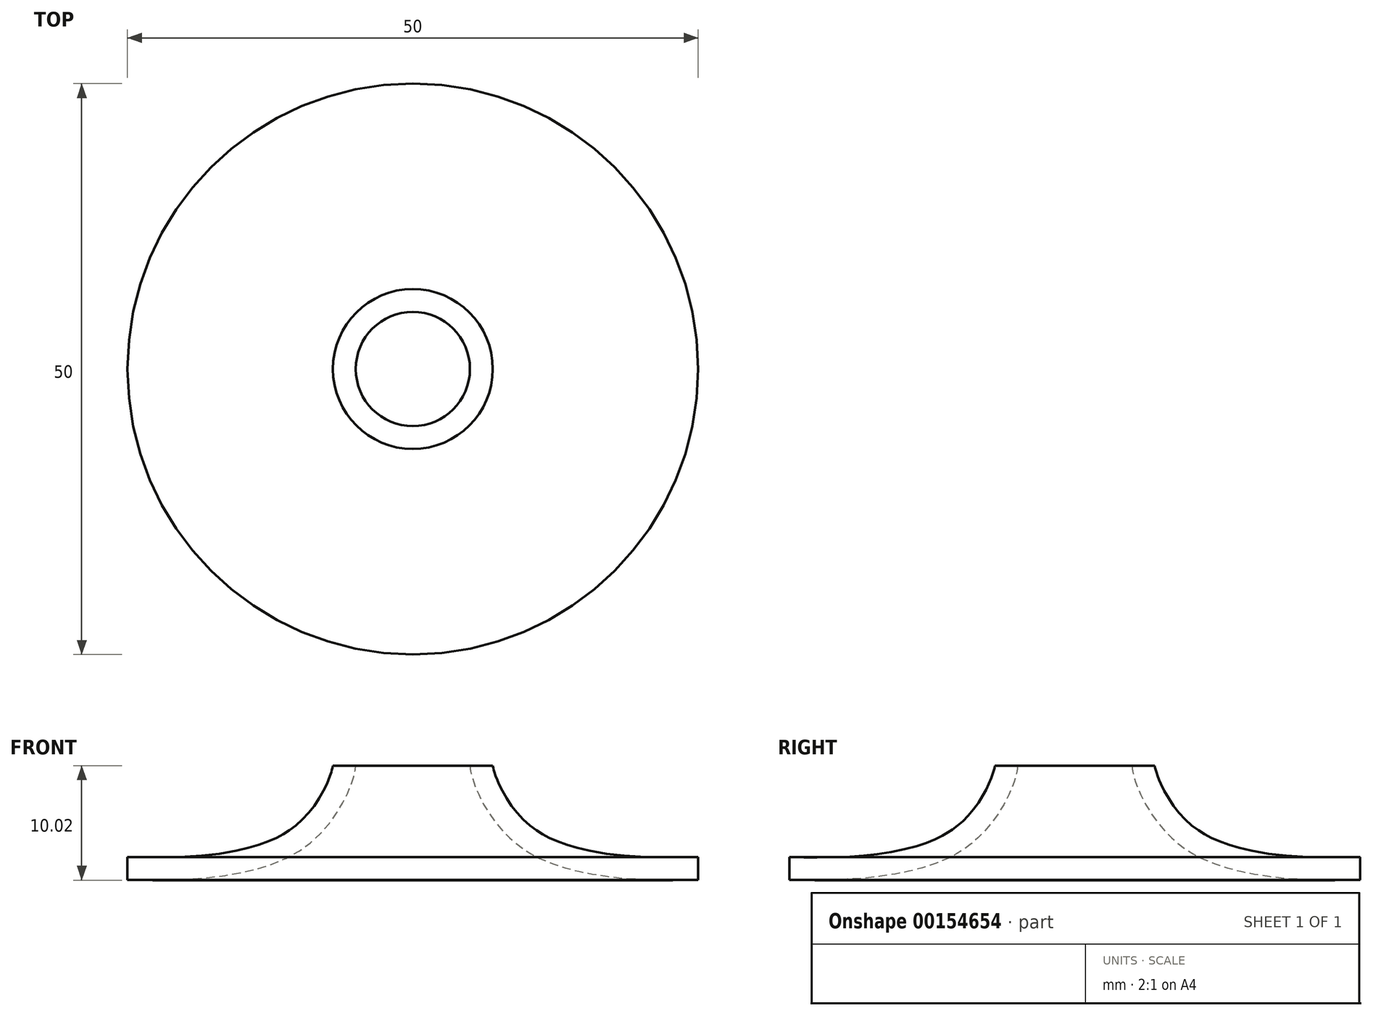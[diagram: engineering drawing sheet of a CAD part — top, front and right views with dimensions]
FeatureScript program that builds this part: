
annotation { "Feature Type Name" : "Feature", "Feature Type Description" : "" }
export const myFeature = defineFeature(function(context is Context, id is Id, definition is map)
    precondition{}
    {
        {
            var Q0;
            Q0=qCreatedBy(makeId("Right.planeOp"),FACE);
            var sketch = newSketch(context, id + "F0", { "sketchPlane" : qUnion([Q0])});
            skLineSegment(sketch, "E0", {"start": v(-25, 0) * mm, "end": v(0, 0) * mm, "construction": true});
            skLineSegment(sketch, "E1", {"start": v(0, 0) * mm, "end": v(0, 10) * mm, "construction": true});
            skLineSegment(sketch, "E2", {"start": v(-5, 0) * mm, "end": v(-5, 10) * mm, "construction": true});
            skFitSpline(sketch, "E3", {"points": [v(-25, 0) * mm, v(-10, 2.5) * mm, v(-5, 10) * mm], "startDerivative": vector(10.62, 0) * mm, "endDerivative": vector(0, 6.9) * mm});
            skFitSpline(sketch, "E4.0", {"points": [v(-25, 2) * mm, v(-24.87, 2) * mm, v(-24.6, 2) * mm, v(-23.94, 1.99) * mm, v(-22.91, 1.97) * mm, v(-21.4, 1.99) * mm, v(-19.12, 2.08) * mm, v(-16.6, 2.34) * mm, v(-14.2, 2.87) * mm, v(-12.82, 3.32) * mm, v(-11.84, 3.75) * mm, v(-11.29, 4.05) * mm, v(-10.89, 4.3) * mm, v(-10.5, 4.58) * mm, v(-10.04, 4.95) * mm, v(-9.54, 5.43) * mm, v(-8.92, 6.12) * mm, v(-8.4, 6.84) * mm, v(-7.97, 7.57) * mm, v(-7.69, 8.1) * mm, v(-7.46, 8.6) * mm, v(-7.27, 9.06) * mm, v(-7.14, 9.47) * mm, v(-7.06, 9.74) * mm, v(-7.03, 9.89) * mm, v(-7.01, 9.95) * mm, v(-7, 10) * mm, v(-7, 10.03) * mm, v(-7, 10.04) * mm, v(-7, 10.04) * mm, v(-7, 10.05) * mm, v(-7, 10.05) * mm, v(-7, 10.05) * mm, v(-7, 10.06) * mm, v(-7, 10.07) * mm, v(-7, 10.1) * mm, v(-7, 10.12) * mm, v(-7, 10.13) * mm]});
            skLineSegment(sketch, "E5", {"start": v(-7, 10) * mm, "end": v(-5, 10) * mm});
            skLineSegment(sketch, "E6", {"start": v(-25, 2) * mm, "end": v(-25, 0) * mm});
            skLineSegment(sketch, "E7", {"start": v(-7, 10) * mm, "end": v(-25, 2) * mm, "construction": true});
            skFitSpline(sketch, "E8", {"points": [v(-44.46, 0) * mm, v(-29.2, 2.5) * mm, v(-24.46, 10) * mm], "startDerivative": vector(10.54, 0) * mm, "endDerivative": vector(0, 6.96) * mm});
            skFitSpline(sketch, "E9.0", {"points": [v(-44.46, 2) * mm, v(-44.33, 2) * mm, v(-44.06, 2) * mm, v(-43.39, 1.98) * mm, v(-42.34, 1.97) * mm, v(-40.8, 1.97) * mm, v(-39.04, 2.04) * mm, v(-37.17, 2.18) * mm, v(-35.28, 2.44) * mm, v(-33.45, 2.84) * mm, v(-32.06, 3.29) * mm, v(-31.08, 3.72) * mm, v(-30.53, 4.02) * mm, v(-30.13, 4.27) * mm, v(-29.75, 4.54) * mm, v(-29.31, 4.91) * mm, v(-28.82, 5.4) * mm, v(-28.23, 6.08) * mm, v(-27.74, 6.8) * mm, v(-27.33, 7.53) * mm, v(-27.08, 8.07) * mm, v(-26.86, 8.57) * mm, v(-26.7, 9.04) * mm, v(-26.57, 9.44) * mm, v(-26.5, 9.72) * mm, v(-26.48, 9.87) * mm, v(-26.47, 9.93) * mm, v(-26.46, 9.97) * mm, v(-26.46, 10) * mm, v(-26.46, 10.02) * mm, v(-26.46, 10.02) * mm, v(-26.46, 10.03) * mm, v(-26.46, 10.03) * mm, v(-26.46, 10.03) * mm, v(-26.46, 10.04) * mm, v(-26.46, 10.05) * mm, v(-26.45, 10.08) * mm, v(-26.45, 10.1) * mm, v(-26.45, 10.1) * mm]});
            skLineSegment(sketch, "E10", {"start": v(-26.46, 10) * mm, "end": v(-24.46, 10) * mm});
            skLineSegment(sketch, "E11", {"start": v(-44.46, 2) * mm, "end": v(-44.46, 0) * mm});
            skLineSegment(sketch, "E12", {"start": v(-26.46, 10) * mm, "end": v(-44.46, 2) * mm, "construction": true});
            skLineSegment(sketch, "E13", {"start": v(-44.46, 0) * mm, "end": v(-24.46, 0) * mm, "construction": true});
            skLineSegment(sketch, "E14", {"start": v(-24.46, 0) * mm, "end": v(-24.46, 10) * mm, "construction": true});
            skSolve(sketch);
        }
        {
            var Q0;
            Q0=makeQuery(id+"F0.imprint","IMPRINT",FACE,{"disambiguationData":[TD([[makeQuery(id+"F0.imprint","IMPRINT",EDGE,{"derivedFrom":sQuery(id+"F0.wireOp",EDGE,"E3")}),1.0]])]});
            var Q1;
            Q1=makeQuery(id+"F0.imprint","IMPRINT",FACE,{"disambiguationData":[TD([[makeQuery(id+"F0.imprint","IMPRINT",EDGE,{"derivedFrom":sQuery(id+"F0.wireOp",EDGE,"E8")}),1.0]])]});
            var Q2;
            Q2=sQuery(id+"F0.wireOp",EDGE,"E1");
            revolve(context, id + "F1", {"entities" : qUnion([Q0, Q1]), "axis" : qUnion([Q2]), "revolveType" : RevolveType.FULL});
        }
    });
